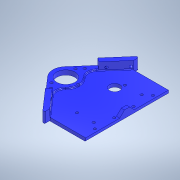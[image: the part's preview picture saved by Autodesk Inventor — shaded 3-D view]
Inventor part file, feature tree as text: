
AUTODESK INVENTOR PART (.ipt)
format: ipt  version: 2022 (Build 260153000, 153)  size: 380,416 bytes
history: native  units: in
note: dims shown in document units (in); Inventor stores cm internally (conversion verified against a paired STEP export)
features: reference x21, sketch x13, extrude x9, other x7, hole x4, projected_geometry x4, fillet x2, mirror x1, chamfer x1
ambient origin geometry x8: Origin, YZ Plane, XZ Plane, XY Plane, X Axis, Y Axis, Z Axis, Center Point
bodies: Solid3 (feature_tree)
feature tree (62):
  extrude  "Extrusion13"  Depth=2.1654in
  extrude  "Extrusion14"  Depth=0.4433in TaperAngle=0.0deg
  mirror  "Mirror4"
  extrude  "Extrusion25"  Depth=0.1969in TaperAngle=0.0deg
  extrude  "Extrusion26"  Depth=1.5748in
  extrude  "Extrusion28"  Depth=0.1969in
  extrude  "Extrusion35"  Depth=0.0787in
  extrude  "Extrusion38"  Depth=1.1024in
  extrude  "Extrusion39"  Depth=0.3937in TaperAngle=0.0deg
  hole  "Hole5"  [1 undecoded]
  fillet  "Fillet3"  Radius=0.4724in
  hole  "Hole6"  [1 undecoded]
  fillet  "Fillet4"  Radius=1.7717in
  chamfer  "Chamfer3"  Distance=0.3937in
  hole  "Hole7"  [1 undecoded]
  hole  "Hole8"  [1 undecoded]
  extrude  "Extrusion40"  Depth=0.0394in TaperAngle=45.0deg
  sketch  "Sketch14"  dims[d94=0.9646in d95=2.1654in]
  sketch  "Sketch15"  dims[d96=1.7717in d97=0.4433in d98=0.0in]
  projected_geometry  "Projected Loop7"
  sketch  "Sketch26"  dims[d99=2.5561in d100=0.1969in d101=0.0in]
  sketch  "Sketch27"  dims[d137=0.7874in d138=1.5748in]
  sketch  "Sketch29"  dims[d139=0.1969in d140=0.0in d141=1.1024in]
  sketch  "Sketch37"  dims[d143=0.0787in d144=0.0in d145=0.5906in]
  projected_geometry  "Projected Loop19"
  sketch  "Sketch40"  dims[d146=1.1024in d149=1.1024in]
  sketch  "Sketch41"  dims[d151=0.6299in d152=0.3937in d153=0.0in]
  projected_geometry  "Projected Loop20"
  sketch  "Sketch42"  dims[d185=0.0in d186=0.0in d198=0.4724in d199=0.4724in]
  reference  "Reference1"
  reference  "Reference2"
  reference  "Reference3"
  reference  "Reference4"
  sketch  "Sketch43"  dims[d200=0.0in d201=0.0in d202=1.5354in d203=1.7717in]
  reference  "Reference5"
  reference  "Reference6"
  reference  "Reference7"
  reference  "Reference8"
  reference  "Reference9"
  reference  "Reference10"
  reference  "Reference11"
  reference  "Reference12"
  reference  "Reference13"
  reference  "Reference14"
  reference  "Reference15"
  reference  "Reference16"
  reference  "Reference17"
  sketch  "Sketch44"  dims[d204=1.8504in]
  reference  "Reference18"
  reference  "Reference19"
  sketch  "Sketch45"  dims[d205=1.8504in d206=0.3937in d207=0.0in]
  reference  "Reference20"
  reference  "Reference21"
  sketch  "Sketch46"  dims[d208=0.1575in d209=0.2362in d210=0.248in d211=0.0787in d212=90.0deg d213=0.315in d214=0.8108in d215=0.0787in d216=0.1575in d217=0.315in d218=0.1575in d219=0.0787in d220=90.0deg d221=0.2756in d222=0.8108in d223=0.0394in d224=0.0394in d225=0.0787in d226=45.0deg d227=0.1575in d228=0.2362in d229=0.248in d230=0.0787in d231=90.0deg d232=0.315in d233=0.8108in d234=0.1575in d235=0.2362in d236=0.1575in d237=0.0787in d238=90.0deg d239=0.315in d240=0.8108in d241=0.2913in d242=0.315in d243=135.0deg d244=0.1969in d245=0.0in d93=0.1575in d107=0.0197in d108=0.0344in d109=0.0197in d110=0.0344in d154=0.0197in d155=0.0344in]
  projected_geometry  "Projected Loop21"
  parser-record x1  (decoder bookkeeping rows leaked as tree rows — omitted from the tree; the rows remain in map.json)
  other  "Main Body.iam"
  other  "ESC Mount:1"
  other  "ESC Mount:2"
  other  "Base Plate:1"
  other  "Front Armor:1"
  other  "Front Armor:2"
note: 4 required parameter values undecoded (feature->parameter linkage not recoverable at this tier; creation-order binding heuristic only, values carry confidence <= 0.55)
note: 1 file-system path scrubbed to <path> (originals preserved in map.json)
